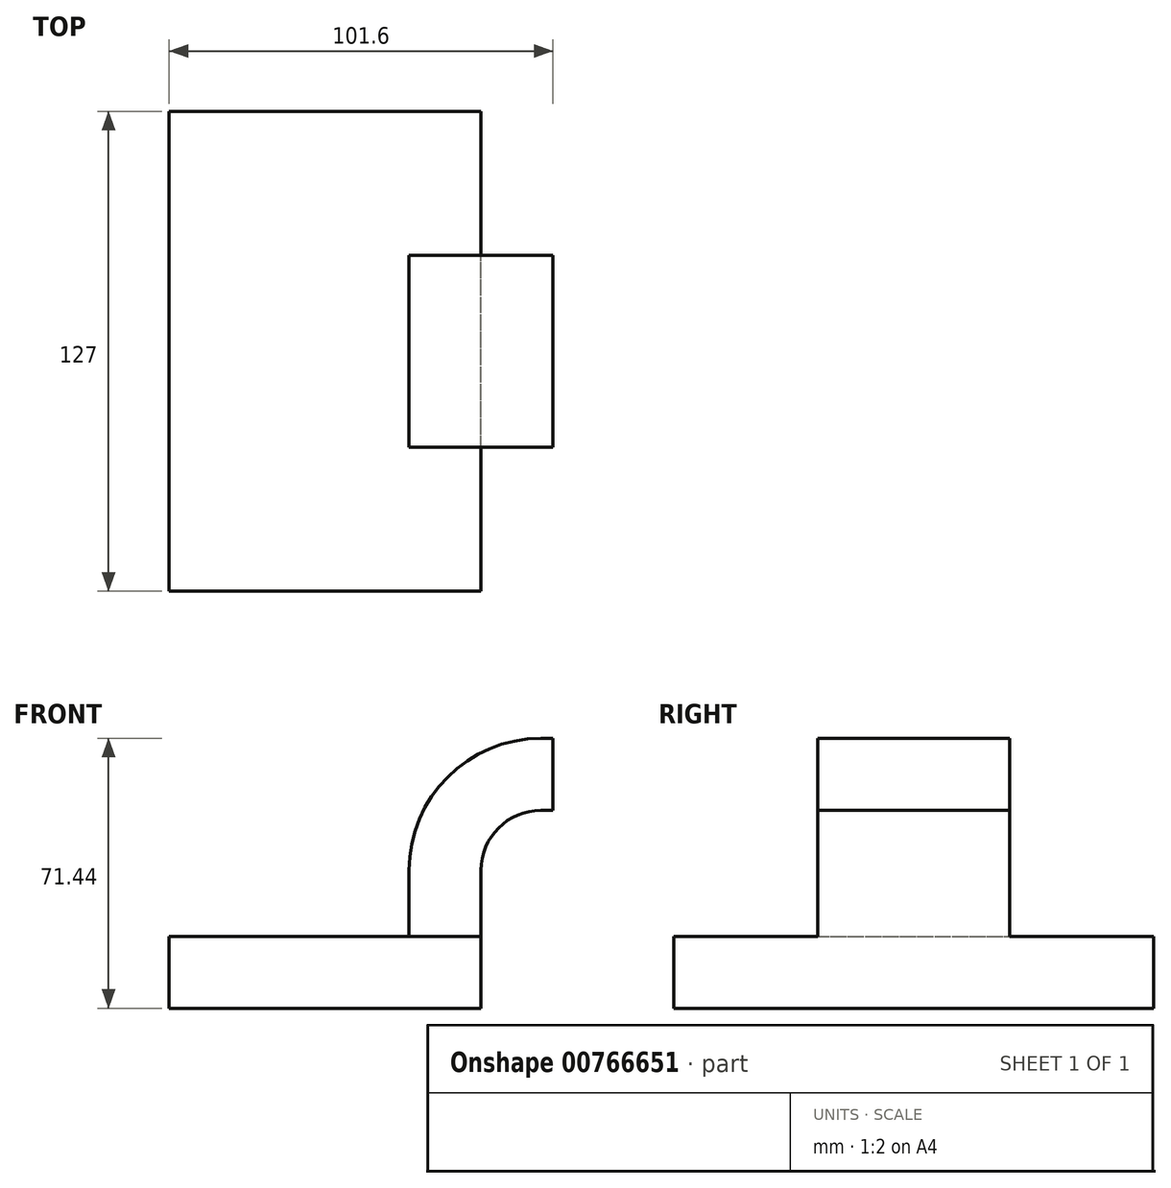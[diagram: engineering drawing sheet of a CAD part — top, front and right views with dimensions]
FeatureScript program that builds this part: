
annotation { "Feature Type Name" : "Feature", "Feature Type Description" : "" }
export const myFeature = defineFeature(function(context is Context, id is Id, definition is map)
    precondition{}
    {
        {
            var Q0;
            Q0=qCreatedBy(makeId("Front.planeOp"),FACE);
            var sketch = newSketch(context, id + "F0", { "sketchPlane" : qUnion([Q0])});
            skLineSegment(sketch, "E0.bottom", {"start": v(41.27, 9.53) * mm, "end": v(-41.28, 9.53) * mm});
            skLineSegment(sketch, "E0.top", {"start": v(41.28, -9.52) * mm, "end": v(-41.27, -9.52) * mm});
            skLineSegment(sketch, "E0.left", {"start": v(41.28, 9.53) * mm, "end": v(41.28, -9.52) * mm});
            skLineSegment(sketch, "E0.right", {"start": v(-41.28, 9.53) * mm, "end": v(-41.28, -9.52) * mm});
            skPoint(sketch, "E0.middle", {"position": v(0, 0) * mm});
            skLineSegment(sketch, "E1.bottom", {"start": v(111.12, 66.68) * mm, "end": v(60.32, 66.68) * mm});
            skLineSegment(sketch, "E1.top", {"start": v(111.12, 38.1) * mm, "end": v(60.33, 38.1) * mm});
            skLineSegment(sketch, "E1.left", {"start": v(111.12, 66.68) * mm, "end": v(111.12, 38.1) * mm});
            skLineSegment(sketch, "E1.right", {"start": v(60.32, 66.68) * mm, "end": v(60.33, 38.1) * mm});
            skPoint(sketch, "E1.middle", {"position": v(85.72, 52.39) * mm});
            skLineSegment(sketch, "E2", {"start": v(41.27, 9.53) * mm, "end": v(41.27, 26.99) * mm});
            skArc(sketch, "E3", {"start": v(41.27, 26.99) * mm, "mid": v(45.92, 38.21) * mm, "end": v(57.15, 42.86) * mm});
            skLineSegment(sketch, "E4", {"start": v(57.15, 42.86) * mm, "end": v(85.72, 42.86) * mm});
            skLineSegment(sketch, "E5.0", {"start": v(57.15, 61.91) * mm, "end": v(85.72, 61.91) * mm});
            skArc(sketch, "E5.1", {"start": v(22.22, 26.99) * mm, "mid": v(32.45, 51.68) * mm, "end": v(57.15, 61.91) * mm});
            skLineSegment(sketch, "E5.2", {"start": v(22.22, 9.53) * mm, "end": v(22.22, 26.99) * mm});
            skLineSegment(sketch, "E6", {"start": v(85.72, 42.86) * mm, "end": v(85.72, 61.91) * mm});
            skFitSpline(sketch, "E7", {"points": [v(-41.28, 9.52) * mm, v(57.15, 61.91) * mm], "startDerivative": vector(36.47, 96.8) * mm, "endDerivative": vector(102.75, -5.84) * mm});
            skSolve(sketch);
        }
        {
            var Q0;
            {var subQ1=sQuery(id+"F0.wireOp",EDGE,"E2");Q0=makeQuery(id+"F0.imprint","IMPRINT",FACE,{"disambiguationData":[TD([[makeQuery(id+"F0.imprint","IMPRINT",EDGE,{"derivedFrom":subQ1}),1.0]])]});}
            extrude(context, id + "F1", {"entities" : qUnion([Q0]), "endBound" : BoundingType.SYMMETRIC, "depth" : 50.8 * mm, "offsetDistance" : 25.4 * mm});
        }
        {
            var Q0;
            Q0=makeQuery(id+"F0.imprint","IMPRINT",FACE,{"disambiguationData":[TD([[makeQuery(id+"F0.imprint","IMPRINT",EDGE,{"derivedFrom":sQuery(id+"F0.wireOp",EDGE,"E0.top")}),-1.0]])]});
            extrude(context, id + "F2", {"entities" : qUnion([Q0]), "operationType" : NewBodyOperationType.ADD, "endBound" : BoundingType.SYMMETRIC, "depth" : 127 * mm, "offsetDistance" : 25.4 * mm});
        }
        {
            var Q0;
            Q0=makeQuery(id+"F0.imprint","IMPRINT",FACE,{"disambiguationData":[TD([[makeQuery(id+"F0.imprint","IMPRINT",EDGE,{"derivedFrom":sQuery(id+"F0.wireOp",EDGE,"E5.1")}),1.0]])]});
            extrude(context, id + "F3", {"entities" : qUnion([Q0]), "operationType" : NewBodyOperationType.ADD, "depth" : 15.88 * mm, "offsetDistance" : 25.4 * mm});
        }
    });
